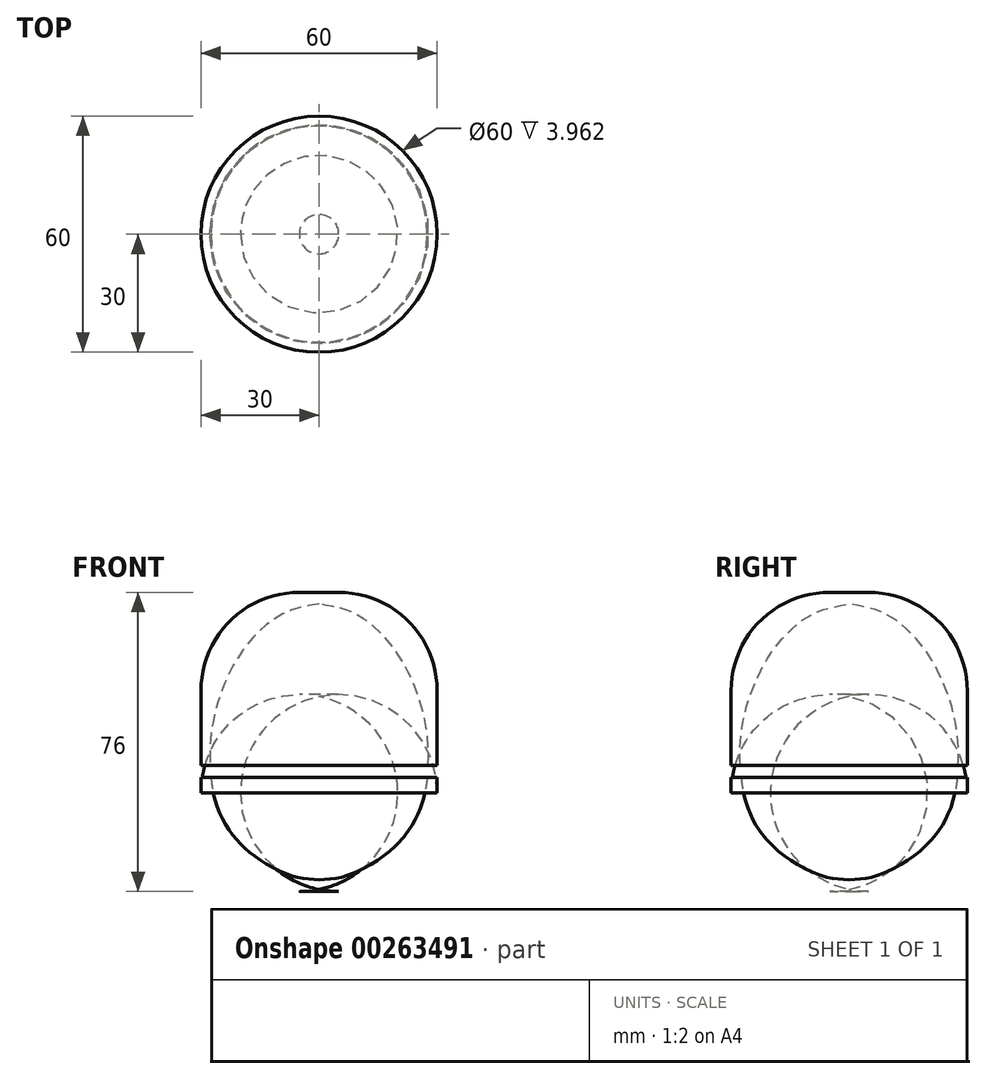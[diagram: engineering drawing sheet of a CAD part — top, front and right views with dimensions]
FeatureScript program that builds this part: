
annotation { "Feature Type Name" : "Feature", "Feature Type Description" : "" }
export const myFeature = defineFeature(function(context is Context, id is Id, definition is map)
    precondition{}
    {
        {
            var Q0;
            Q0=qCreatedBy(makeId("Front.planeOp"),FACE);
            var sketch = newSketch(context, id + "F0", { "sketchPlane" : qUnion([Q0])});
            skFitSpline(sketch, "E0", {"points": [v(0, 46.43) * mm, v(-8.86, 44.14) * mm, v(-16.29, 38.43) * mm, v(-20.86, 32.43) * mm, v(-25.14, 23.29) * mm, v(-27.43, 13.57) * mm, v(-27.71, 6.14) * mm, v(-26.29, -3.86) * mm, v(-22, -12.14) * mm, v(-16, -17.86) * mm, v(-6.57, -22.71) * mm, v(0, -23.57) * mm], "startDerivative": vector(-98.81, -15.48) * mm, "endDerivative": vector(79.6, -2.58) * mm});
            skLineSegment(sketch, "E1", {"start": v(0, 46.43) * mm, "end": v(0, -23.57) * mm});
            skPoint(sketch, "E2", {"position": v(-27.68, 5.4) * mm});
            skLineSegment(sketch, "E3", {"start": v(-30, 48.2) * mm, "end": v(-30, 5.4) * mm});
            skLineSegment(sketch, "E4", {"start": v(-30, -21.8) * mm, "end": v(-30, 2.4) * mm});
            skLineSegment(sketch, "E5", {"start": v(0, 46.43) * mm, "end": v(0, 49.43) * mm});
            skLineSegment(sketch, "E6", {"start": v(0, 49.43) * mm, "end": v(-30, 49.43) * mm});
            skLineSegment(sketch, "E7", {"start": v(-30, 49.43) * mm, "end": v(-30, 48.2) * mm});
            skLineSegment(sketch, "E8", {"start": v(0, -23.57) * mm, "end": v(0, -26.57) * mm});
            skLineSegment(sketch, "E9", {"start": v(0, -26.57) * mm, "end": v(-30, -26.57) * mm});
            skLineSegment(sketch, "E10", {"start": v(-30, -26.57) * mm, "end": v(-30, -21.8) * mm});
            skLineSegment(sketch, "E11", {"start": v(-30, 2.4) * mm, "end": v(-27.46, 2.4) * mm});
            skLineSegment(sketch, "E12", {"start": v(-30, 5.4) * mm, "end": v(-27.68, 5.4) * mm});
            skSolve(sketch);
        }
        {
            var Q0;
            Q0=makeQuery(id+"F0.imprint","IMPRINT",FACE,{"disambiguationData":[TD([[makeQuery(id+"F0.imprint","IMPRINT",EDGE,{"derivedFrom":sQuery(id+"F0.wireOp",EDGE,"E3")}),1.0]])]});
            var Q1;
            Q1=sQuery(id+"F0.wireOp",EDGE,"E1");
            revolve(context, id + "F1", {"entities" : qUnion([Q0]), "axis" : qUnion([Q1]), "revolveType" : RevolveType.FULL});
        }
        {
            var Q0;
            Q0=makeQuery(id+"F1.opRevolve","SWEPT_EDGE",EDGE,{"disambiguationData":[OSD([sQuery(id+"F0.wireOp",EDGE,"E6"),sQuery(id+"F0.wireOp",EDGE,"E7")])]});
            fillet(context, id + "F2", {"entities" : qUnion([Q0]), "radius" : 25 * mm, "tangentPropagation" : true, "allowEdgeOverflow" : false});
        }
        {
            var Q0;
            Q0=makeQuery(id+"F0.imprint","IMPRINT",FACE,{"disambiguationData":[TD([[makeQuery(id+"F0.imprint","IMPRINT",EDGE,{"derivedFrom":sQuery(id+"F0.wireOp",EDGE,"E4")}),-1.0]])]});
            var Q1;
            Q1=sQuery(id+"F0.wireOp",EDGE,"E1");
            revolve(context, id + "F3", {"entities" : qUnion([Q0]), "axis" : qUnion([Q1]), "revolveType" : RevolveType.FULL});
        }
        {
            var Q0;
            Q0=makeQuery(id+"F3.opRevolve","SWEPT_EDGE",EDGE,{"disambiguationData":[OSD([sQuery(id+"F0.wireOp",EDGE,"E9"),sQuery(id+"F0.wireOp",EDGE,"E10")])]});
            fillet(context, id + "F4", {"entities" : qUnion([Q0]), "radius" : 25 * mm, "tangentPropagation" : true, "allowEdgeOverflow" : false});
        }
    });
